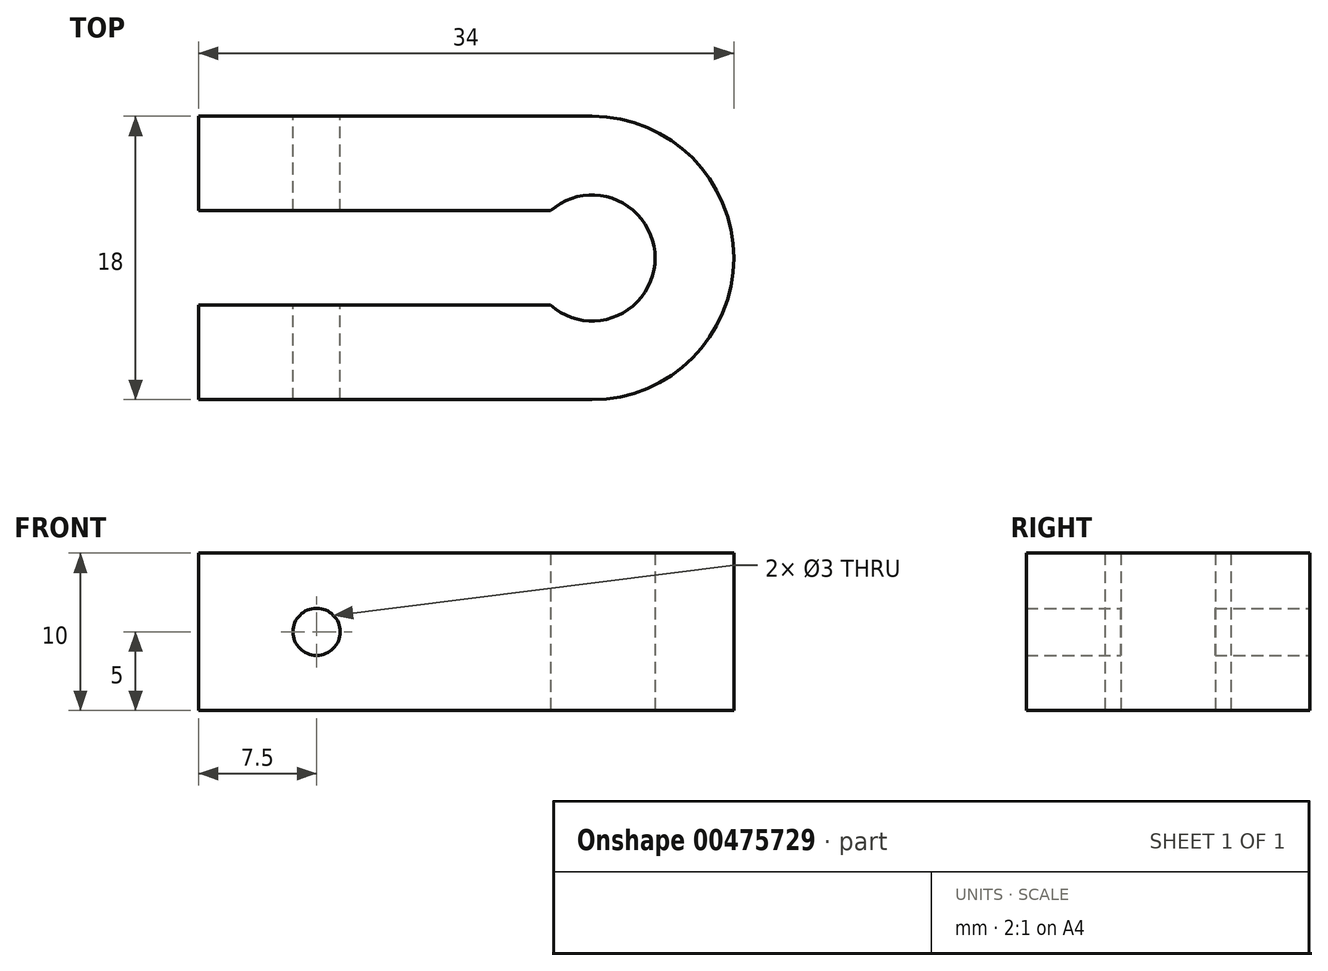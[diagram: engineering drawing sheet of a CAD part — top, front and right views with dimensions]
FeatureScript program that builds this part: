
annotation { "Feature Type Name" : "Feature", "Feature Type Description" : "" }
export const myFeature = defineFeature(function(context is Context, id is Id, definition is map)
    precondition{}
    {
        {
            var Q0;
            Q0=qCreatedBy(makeId("Top.planeOp"),FACE);
            var sketch = newSketch(context, id + "F0", { "sketchPlane" : qUnion([Q0])});
            skCircle(sketch, "E0", {"center": v(0, 0) * mm, "radius": 4 * mm});
            skCircle(sketch, "E1", {"center": v(0, 0) * mm, "radius": 9 * mm});
            skLineSegment(sketch, "E2.bottom", {"start": v(0, 9) * mm, "end": v(-25, 9) * mm});
            skLineSegment(sketch, "E2.top", {"start": v(0, 3) * mm, "end": v(-25, 3) * mm});
            skLineSegment(sketch, "E2.left", {"start": v(0, 9) * mm, "end": v(0, 3) * mm});
            skLineSegment(sketch, "E2.right", {"start": v(-25, 9) * mm, "end": v(-25, 3) * mm});
            skLineSegment(sketch, "E3.bottom", {"start": v(0, -9) * mm, "end": v(-25, -9) * mm});
            skLineSegment(sketch, "E3.top", {"start": v(0, -3) * mm, "end": v(-25, -3) * mm});
            skLineSegment(sketch, "E3.left", {"start": v(0, -9) * mm, "end": v(0, -3) * mm});
            skLineSegment(sketch, "E3.right", {"start": v(-25, -9) * mm, "end": v(-25, -3) * mm});
            skSolve(sketch);
        }
        {
            var Q0;
            {var subQ0=sQuery(id+"F0.wireOp",EDGE,"E2.left");var subQ1=sQuery(id+"F0.wireOp",EDGE,"E0");var subQ2=makeQuery(id+"F0.imprint","INTERSECT",VERTEX,{"derivedFrom":[subQ1,subQ0]});Q0=makeQuery(id+"F0.imprint","IMPRINT",FACE,{"disambiguationData":[TD([[makeQuery(id+"F0.imprint","IMPRINT",EDGE,{"disambiguationData":[TD([[subQ2,1.0]])],"derivedFrom":subQ1}),-1.0]])]});}
            var Q1;
            {var subQ0=sQuery(id+"F0.wireOp",EDGE,"E2.top");var subQ1=sQuery(id+"F0.wireOp",EDGE,"E0");var subQ2=makeQuery(id+"F0.imprint","INTERSECT",VERTEX,{"derivedFrom":[subQ1,subQ0]});Q1=makeQuery(id+"F0.imprint","IMPRINT",FACE,{"disambiguationData":[TD([[makeQuery(id+"F0.imprint","IMPRINT",EDGE,{"disambiguationData":[TD([[subQ2,1.0]])],"derivedFrom":subQ1}),-1.0]])]});}
            var Q2;
            {var subQ0=sQuery(id+"F0.wireOp",EDGE,"E2.bottom");Q2=makeQuery(id+"F0.imprint","IMPRINT",FACE,{"disambiguationData":[TD([[makeQuery(id+"F0.imprint","IMPRINT",EDGE,{"derivedFrom":subQ0}),1.0]])]});}
            var Q3;
            {var subQ0=sQuery(id+"F0.wireOp",EDGE,"E3.bottom");Q3=makeQuery(id+"F0.imprint","IMPRINT",FACE,{"disambiguationData":[TD([[makeQuery(id+"F0.imprint","IMPRINT",EDGE,{"derivedFrom":subQ0}),-1.0]])]});}
            var Q4;
            {var subQ0=sQuery(id+"F0.wireOp",EDGE,"E3.top");var subQ1=sQuery(id+"F0.wireOp",EDGE,"E0");var subQ2=makeQuery(id+"F0.imprint","INTERSECT",VERTEX,{"derivedFrom":[subQ1,subQ0]});Q4=makeQuery(id+"F0.imprint","IMPRINT",FACE,{"disambiguationData":[TD([[makeQuery(id+"F0.imprint","IMPRINT",EDGE,{"disambiguationData":[TD([[subQ2,-1.0]])],"derivedFrom":subQ1}),-1.0]])]});}
            extrude(context, id + "F1", {"entities" : qUnion([Q0, Q1, Q2, Q3, Q4]), "depth" : 10 * mm});
        }
        {
            var Q0;
            Q0=makeQuery(id+"F1.opExtrude","SWEPT_FACE",FACE,{"disambiguationData":[OSD([sQuery(id+"F0.wireOp",EDGE,"E2.bottom")])]});
            var sketch = newSketch(context, id + "F2", { "sketchPlane" : qUnion([Q0])});
            skCircle(sketch, "E4", {"center": v(17.5, 5) * mm, "radius": 1.5 * mm});
            skPoint(sketch, "E4.centerSnap0", {"position": v(25, 5) * mm});
            skSolve(sketch);
        }
        {
            var Q0;
            Q0=qSketchRegion(id+"F2",true);
            extrude(context, id + "F3", {"entities" : qUnion([Q0]), "operationType" : NewBodyOperationType.REMOVE, "endBound" : BoundingType.THROUGH_ALL, "oppositeDirection" : true, "depth" : 25 * mm});
        }
    });
